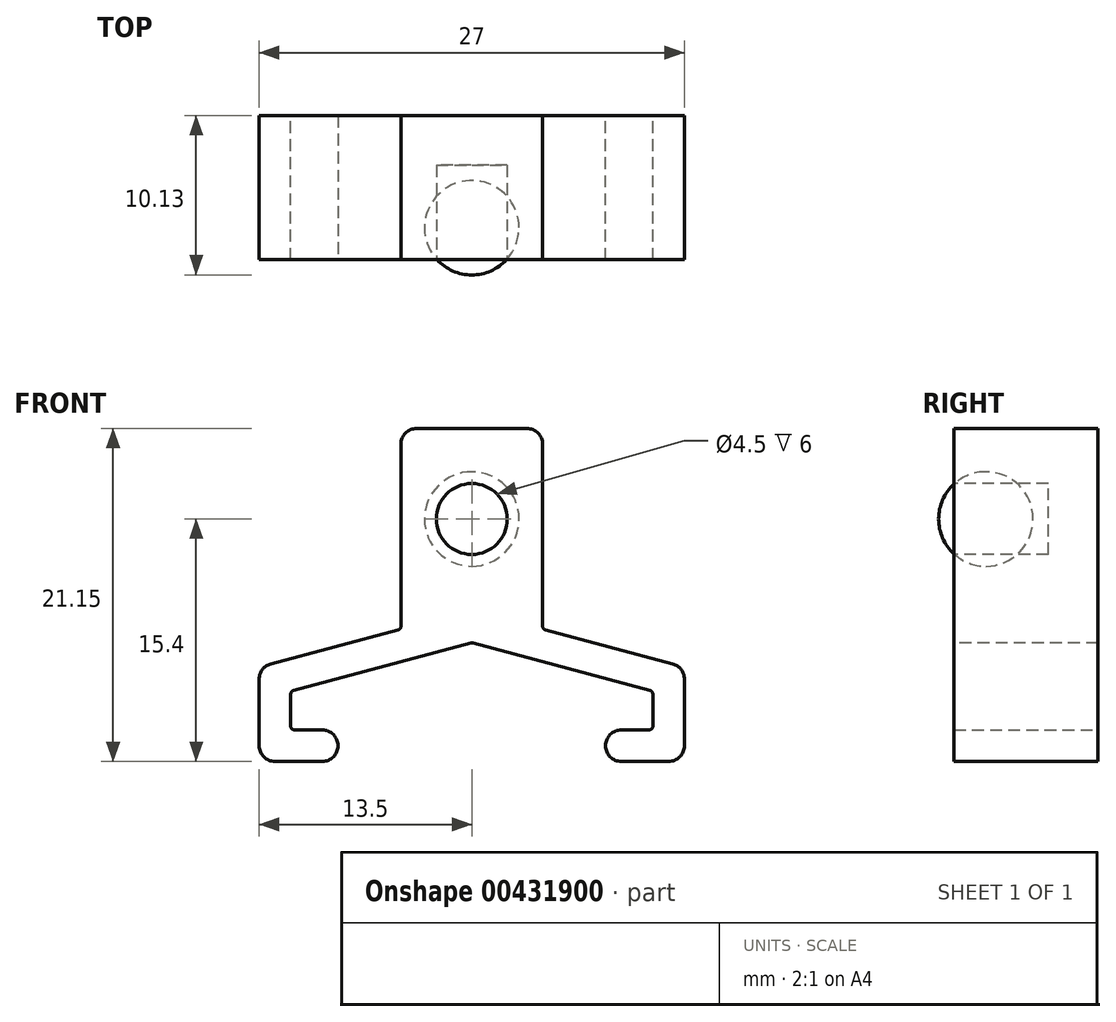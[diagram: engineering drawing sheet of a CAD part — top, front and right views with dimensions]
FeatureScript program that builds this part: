
annotation { "Feature Type Name" : "Feature", "Feature Type Description" : "" }
export const myFeature = defineFeature(function(context is Context, id is Id, definition is map)
    precondition{}
    {
        {
            var Q0;
            Q0=qCreatedBy(makeId("Front.planeOp"),FACE);
            var sketch = newSketch(context, id + "F0", { "sketchPlane" : qUnion([Q0])});
            skLineSegment(sketch, "E0.bottom", {"start": v(-13.5, -3) * mm, "end": v(-8.5, -3) * mm});
            skLineSegment(sketch, "E0.left", {"start": v(-13.5, -3) * mm, "end": v(-13.5, 3) * mm});
            skLineSegment(sketch, "E0.right", {"start": v(13.5, -3) * mm, "end": v(13.5, 3) * mm});
            skPoint(sketch, "E0.middle", {"position": v(0, 0) * mm});
            skLineSegment(sketch, "E1.top", {"start": v(4.5, 18.15) * mm, "end": v(-4.5, 18.15) * mm});
            skLineSegment(sketch, "E1.left", {"start": v(4.5, 5.4) * mm, "end": v(4.5, 18.15) * mm});
            skLineSegment(sketch, "E1.right", {"start": v(-4.5, 5.4) * mm, "end": v(-4.5, 18.15) * mm});
            skPoint(sketch, "E1.middle", {"position": v(0, 11.78) * mm});
            skLineSegment(sketch, "E2", {"start": v(4.5, 5.4) * mm, "end": v(13.5, 3) * mm});
            skLineSegment(sketch, "E3", {"start": v(-13.5, 3) * mm, "end": v(-4.5, 5.4) * mm});
            skLineSegment(sketch, "E4.0", {"start": v(-11.5, -1) * mm, "end": v(-8.5, -1) * mm});
            skLineSegment(sketch, "E5.0", {"start": v(-11.5, -1) * mm, "end": v(-11.5, 1.46) * mm});
            skLineSegment(sketch, "E6.0", {"start": v(-11.5, 1.46) * mm, "end": v(0, 4.53) * mm});
            skLineSegment(sketch, "E7.0", {"start": v(0, 4.53) * mm, "end": v(11.5, 1.46) * mm});
            skLineSegment(sketch, "E8.0", {"start": v(11.5, -1) * mm, "end": v(11.5, 1.46) * mm});
            skLineSegment(sketch, "E9", {"start": v(-8.5, -1) * mm, "end": v(-8.5, -3) * mm});
            skLineSegment(sketch, "E10.MirrorCS", {"start": v(8.5, -1) * mm, "end": v(8.5, -3) * mm});
            skLineSegment(sketch, "E11.trimOffspring", {"start": v(8.5, -1) * mm, "end": v(11.5, -1) * mm});
            skLineSegment(sketch, "E12.trimOffspring", {"start": v(8.5, -3) * mm, "end": v(13.5, -3) * mm});
            skSolve(sketch);
        }
        {
            var Q0;
            Q0=makeQuery(id+"F0.imprint","IMPRINT",FACE,{"disambiguationData":[TD([[makeQuery(id+"F0.imprint","IMPRINT",EDGE,{"derivedFrom":sQuery(id+"F0.wireOp",EDGE,"E0.bottom")}),1.0]])]});
            extrude(context, id + "F1", {"entities" : qUnion([Q0]), "depth" : 4.58 * mm, "hasSecondDirection" : true, "secondDirectionOppositeDirection" : true, "secondDirectionDepth" : 4.58 * mm});
        }
        {
            var Q0;
            Q0=makeQuery(id+"F1.opExtrude","CAP_FACE",FACE,{"disambiguationData":[OSD([sQuery(id+"F0.wireOp",EDGE,"E0.bottom"),sQuery(id+"F0.wireOp",EDGE,"E0.left"),sQuery(id+"F0.wireOp",EDGE,"E0.right"),sQuery(id+"F0.wireOp",EDGE,"E1.top"),sQuery(id+"F0.wireOp",EDGE,"E1.left"),sQuery(id+"F0.wireOp",EDGE,"E1.right"),sQuery(id+"F0.wireOp",EDGE,"E2"),sQuery(id+"F0.wireOp",EDGE,"E3"),sQuery(id+"F0.wireOp",EDGE,"E4.0"),sQuery(id+"F0.wireOp",EDGE,"E5.0"),sQuery(id+"F0.wireOp",EDGE,"E6.0"),sQuery(id+"F0.wireOp",EDGE,"E7.0"),sQuery(id+"F0.wireOp",EDGE,"E8.0"),sQuery(id+"F0.wireOp",EDGE,"E9"),sQuery(id+"F0.wireOp",EDGE,"E10.MirrorCS"),sQuery(id+"F0.wireOp",EDGE,"E11.trimOffspring"),sQuery(id+"F0.wireOp",EDGE,"E12.trimOffspring")])],"isStart":false});
            var sketch = newSketch(context, id + "F2", { "sketchPlane" : qUnion([Q0])});
            skCircle(sketch, "E13", {"center": v(0, 12.4) * mm, "radius": 2.25 * mm});
            skSolve(sketch);
        }
        {
            var Q0;
            Q0=makeQuery(id+"F2.imprint","IMPRINT",FACE,{"disambiguationData":[TD([[makeQuery(id+"F2.imprint","IMPRINT",EDGE,{"derivedFrom":sQuery(id+"F2.wireOp",EDGE,"E13")}),1.0]])]});
            extrude(context, id + "F3", {"entities" : qUnion([Q0]), "operationType" : NewBodyOperationType.REMOVE, "oppositeDirection" : true, "depth" : 6 * mm});
        }
        {
            var Q0;
            Q0=makeQuery(id+"F1.opExtrude","SWEPT_EDGE",EDGE,{"disambiguationData":[OSD([sQuery(id+"F0.wireOp",EDGE,"E1.top"),sQuery(id+"F0.wireOp",EDGE,"E1.right")])]});
            var Q1;
            Q1=makeQuery(id+"F1.opExtrude","SWEPT_EDGE",EDGE,{"disambiguationData":[OSD([sQuery(id+"F0.wireOp",EDGE,"E1.top"),sQuery(id+"F0.wireOp",EDGE,"E1.left")])]});
            var Q2;
            Q2=makeQuery(id+"F1.opExtrude","SWEPT_EDGE",EDGE,{"disambiguationData":[OSD([sQuery(id+"F0.wireOp",EDGE,"E0.right"),sQuery(id+"F0.wireOp",EDGE,"E2")])]});
            var Q3;
            Q3=makeQuery(id+"F1.opExtrude","SWEPT_EDGE",EDGE,{"disambiguationData":[OSD([sQuery(id+"F0.wireOp",EDGE,"E0.right"),sQuery(id+"F0.wireOp",EDGE,"E12.trimOffspring")])]});
            var Q4;
            Q4=makeQuery(id+"F1.opExtrude","SWEPT_EDGE",EDGE,{"disambiguationData":[OSD([sQuery(id+"F0.wireOp",EDGE,"E10.MirrorCS"),sQuery(id+"F0.wireOp",EDGE,"E12.trimOffspring")])]});
            var Q5;
            Q5=makeQuery(id+"F1.opExtrude","SWEPT_EDGE",EDGE,{"disambiguationData":[OSD([sQuery(id+"F0.wireOp",EDGE,"E10.MirrorCS"),sQuery(id+"F0.wireOp",EDGE,"E11.trimOffspring")])]});
            var Q6;
            Q6=makeQuery(id+"F1.opExtrude","SWEPT_EDGE",EDGE,{"disambiguationData":[OSD([sQuery(id+"F0.wireOp",EDGE,"E0.bottom"),sQuery(id+"F0.wireOp",EDGE,"E9")])]});
            var Q7;
            Q7=makeQuery(id+"F1.opExtrude","SWEPT_EDGE",EDGE,{"disambiguationData":[OSD([sQuery(id+"F0.wireOp",EDGE,"E4.0"),sQuery(id+"F0.wireOp",EDGE,"E9")])]});
            var Q8;
            Q8=makeQuery(id+"F1.opExtrude","SWEPT_EDGE",EDGE,{"disambiguationData":[OSD([sQuery(id+"F0.wireOp",EDGE,"E0.left"),sQuery(id+"F0.wireOp",EDGE,"E3")])]});
            var Q9;
            Q9=makeQuery(id+"F1.opExtrude","SWEPT_EDGE",EDGE,{"disambiguationData":[OSD([sQuery(id+"F0.wireOp",EDGE,"E0.bottom"),sQuery(id+"F0.wireOp",EDGE,"E0.left")])]});
            fillet(context, id + "F4", {"entities" : qUnion([Q0, Q1, Q2, Q3, Q4, Q5, Q6, Q7, Q8, Q9]), "radius" : 1 * mm, "tangentPropagation" : true, "allowEdgeOverflow" : false});
        }
        {
            var Q0;
            Q0=makeQuery(id+"F1.opExtrude","SWEPT_EDGE",EDGE,{"disambiguationData":[OSD([sQuery(id+"F0.wireOp",EDGE,"E1.left"),sQuery(id+"F0.wireOp",EDGE,"E2")])]});
            var Q1;
            Q1=makeQuery(id+"F1.opExtrude","SWEPT_EDGE",EDGE,{"disambiguationData":[OSD([sQuery(id+"F0.wireOp",EDGE,"E4.0"),sQuery(id+"F0.wireOp",EDGE,"E5.0")])]});
            var Q2;
            Q2=makeQuery(id+"F1.opExtrude","SWEPT_EDGE",EDGE,{"disambiguationData":[OSD([sQuery(id+"F0.wireOp",EDGE,"E5.0"),sQuery(id+"F0.wireOp",EDGE,"E6.0")])]});
            var Q3;
            Q3=makeQuery(id+"F1.opExtrude","SWEPT_EDGE",EDGE,{"disambiguationData":[OSD([sQuery(id+"F0.wireOp",EDGE,"E8.0"),sQuery(id+"F0.wireOp",EDGE,"E11.trimOffspring")])]});
            var Q4;
            Q4=makeQuery(id+"F1.opExtrude","SWEPT_EDGE",EDGE,{"disambiguationData":[OSD([sQuery(id+"F0.wireOp",EDGE,"E7.0"),sQuery(id+"F0.wireOp",EDGE,"E8.0")])]});
            var Q5;
            Q5=makeQuery(id+"F1.opExtrude","SWEPT_EDGE",EDGE,{"disambiguationData":[OSD([sQuery(id+"F0.wireOp",EDGE,"E6.0"),sQuery(id+"F0.wireOp",EDGE,"E7.0")])]});
            var Q6;
            Q6=makeQuery(id+"F1.opExtrude","SWEPT_EDGE",EDGE,{"disambiguationData":[OSD([sQuery(id+"F0.wireOp",EDGE,"E1.right"),sQuery(id+"F0.wireOp",EDGE,"E3")])]});
            fillet(context, id + "F5", {"entities" : qUnion([Q0, Q1, Q2, Q3, Q4, Q5, Q6]), "radius" : .25 * mm, "tangentPropagation" : true, "allowEdgeOverflow" : false});
        }
        {
            var Q0;
            Q0=qCreatedBy(makeId("Front.planeOp"),FACE);
            cPlane(context, id + "F6", {"entities" : qUnion([Q0]), "cplaneType" : CPlaneType.OFFSET, "offset" : 2.55 * mm, "width" : 150 * mm, "height" : 150 * mm});
        }
        {
            var Q0;
            Q0=qCreatedBy(id+"F6.planeOp",FACE);
            var sketch = newSketch(context, id + "F7", { "sketchPlane" : qUnion([Q0])});
            skArc(sketch, "E14", {"start": v(0, 9.4) * mm, "mid": v(3, 12.4) * mm, "end": v(0, 15.4) * mm});
            skLineSegment(sketch, "E15", {"start": v(0, 15.4) * mm, "end": v(0, 9.4) * mm});
            skSolve(sketch);
        }
        {
            var Q0;
            Q0 = qSketchRegion(id + "F7", true);
            var Q1;
            Q1=sQuery(id+"F7.wireOp",EDGE,"E15");
            revolve(context, id + "F8", {"entities" : qUnion([Q0]), "axis" : qUnion([Q1]), "revolveType" : RevolveType.FULL});
        }
    });
